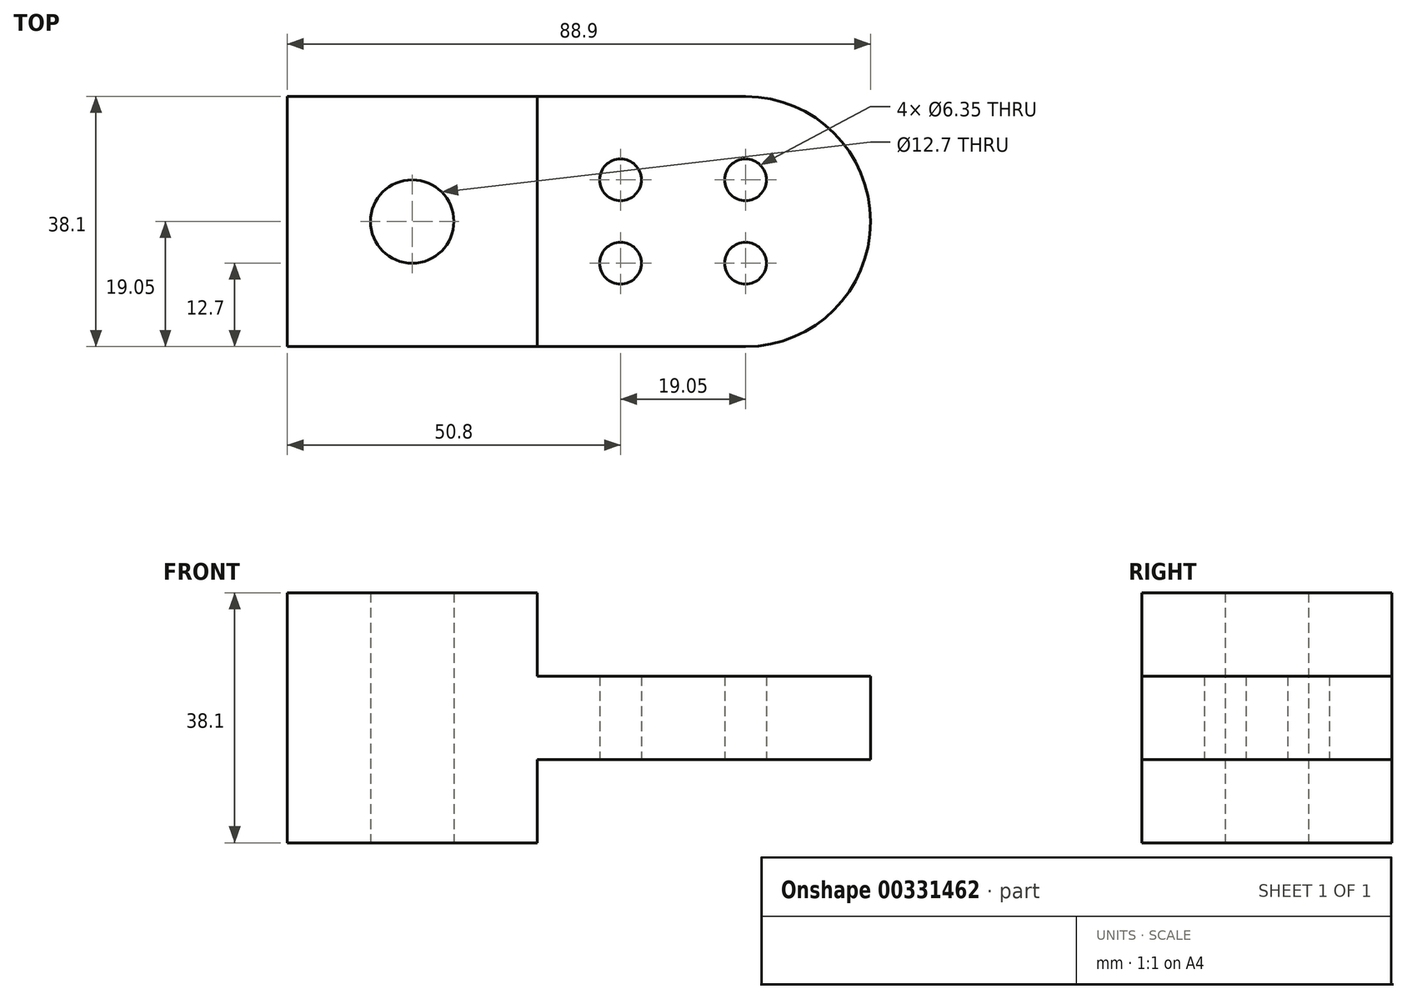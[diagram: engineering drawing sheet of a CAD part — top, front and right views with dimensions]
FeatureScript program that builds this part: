
annotation { "Feature Type Name" : "Feature", "Feature Type Description" : "" }
export const myFeature = defineFeature(function(context is Context, id is Id, definition is map)
    precondition{}
    {
        {
            var Q0;
            Q0=qCreatedBy(makeId("Top.planeOp"),FACE);
            var sketch = newSketch(context, id + "F0", { "sketchPlane" : qUnion([Q0])});
            skLineSegment(sketch, "E0", {"start": v(0, 0) * mm, "end": v(0, 38.1) * mm});
            skLineSegment(sketch, "E1", {"start": v(0, 38.1) * mm, "end": v(38.1, 38.1) * mm});
            skLineSegment(sketch, "E2", {"start": v(38.1, 38.1) * mm, "end": v(38.1, 0) * mm});
            skLineSegment(sketch, "E3", {"start": v(38.1, 0) * mm, "end": v(0, 0) * mm});
            skLineSegment(sketch, "E4", {"start": v(38.1, 38.1) * mm, "end": v(69.85, 38.1) * mm});
            skLineSegment(sketch, "E5", {"start": v(38.1, 0) * mm, "end": v(69.85, 0) * mm});
            skLineSegment(sketch, "E6", {"start": v(69.85, 9.53) * mm, "end": v(69.85, 15.88) * mm, "construction": true});
            skArc(sketch, "E7", {"start": v(69.85, 0) * mm, "mid": v(88.9, 19.05) * mm, "end": v(69.85, 38.1) * mm});
            skLineSegment(sketch, "E8", {"start": v(19.05, 0) * mm, "end": v(19.05, 38.1) * mm, "construction": true});
            skCircle(sketch, "E9", {"center": v(19.05, 19.05) * mm, "radius": 6.35 * mm});
            skLineSegment(sketch, "E10", {"start": v(50.8, 38.1) * mm, "end": v(50.8, 9.53) * mm, "construction": true});
            skCircle(sketch, "E11", {"center": v(50.8, 25.4) * mm, "radius": 3.18 * mm});
            skCircle(sketch, "E12", {"center": v(69.85, 25.4) * mm, "radius": 3.18 * mm});
            skCircle(sketch, "E13", {"center": v(69.85, 12.7) * mm, "radius": 3.18 * mm});
            skCircle(sketch, "E14", {"center": v(50.8, 12.7) * mm, "radius": 3.18 * mm});
            skPoint(sketch, "E15.orphan", {"position": v(50.8, 0) * mm});
            skLineSegment(sketch, "E16.trimOffspring", {"start": v(69.85, 22.23) * mm, "end": v(69.85, 28.58) * mm, "construction": true});
            skSolve(sketch);
        }
        {
            var Q0;
            Q0 = qSketchRegion(id + "F0", true);
            extrude(context, id + "F1", {"entities" : qUnion([Q0]), "depth" : 12.7 * mm});
        }
        {
            var Q0;
            Q0=makeQuery(id+"F1.opExtrude","CAP_FACE",FACE,{"disambiguationData":[OSD([sQuery(id+"F0.wireOp",EDGE,"E0"),sQuery(id+"F0.wireOp",EDGE,"E1"),sQuery(id+"F0.wireOp",EDGE,"E3"),sQuery(id+"F0.wireOp",EDGE,"E4"),sQuery(id+"F0.wireOp",EDGE,"E5"),sQuery(id+"F0.wireOp",EDGE,"E7"),sQuery(id+"F0.wireOp",EDGE,"E9"),sQuery(id+"F0.wireOp",EDGE,"E11"),sQuery(id+"F0.wireOp",EDGE,"E12"),sQuery(id+"F0.wireOp",EDGE,"E13"),sQuery(id+"F0.wireOp",EDGE,"E14")])],"isStart":false});
            var sketch = newSketch(context, id + "F2", { "sketchPlane" : qUnion([Q0])});
            skLineSegment(sketch, "E17", {"start": v(38.1, 38.1) * mm, "end": v(38.1, 0) * mm});
            skSolve(sketch);
        }
        {
            var Q0;
            Q0 = qSketchRegion(id + "F2", true);
            var Q1;
            {var subQ2=sQuery(id+"F2.wireOp",EDGE,"E17");Q1=makeQuery(id+"F2.imprint","IMPRINT",FACE,{"disambiguationData":[TD([[makeQuery(id+"F2.imprint","IMPRINT",EDGE,{"derivedFrom":subQ2}),-1.0]])]});}
            extrude(context, id + "F3", {"entities" : qUnion([Q0, Q1]), "operationType" : NewBodyOperationType.ADD, "depth" : 12.7 * mm});
        }
        {
            var Q0;
            Q0=makeQuery(id+"F1.opExtrude","CAP_FACE",FACE,{"disambiguationData":[OSD([sQuery(id+"F0.wireOp",EDGE,"E0"),sQuery(id+"F0.wireOp",EDGE,"E1"),sQuery(id+"F0.wireOp",EDGE,"E3"),sQuery(id+"F0.wireOp",EDGE,"E4"),sQuery(id+"F0.wireOp",EDGE,"E5"),sQuery(id+"F0.wireOp",EDGE,"E7"),sQuery(id+"F0.wireOp",EDGE,"E9"),sQuery(id+"F0.wireOp",EDGE,"E11"),sQuery(id+"F0.wireOp",EDGE,"E12"),sQuery(id+"F0.wireOp",EDGE,"E13"),sQuery(id+"F0.wireOp",EDGE,"E14")])],"isStart":true});
            var sketch = newSketch(context, id + "F4", { "sketchPlane" : qUnion([Q0])});
            skLineSegment(sketch, "E18", {"start": v(38.1, 0) * mm, "end": v(38.1, -38.1) * mm});
            skSolve(sketch);
        }
        {
            var Q0;
            Q0 = qSketchRegion(id + "F4", true);
            var Q1;
            {var subQ2=sQuery(id+"F4.wireOp",EDGE,"E18");Q1=makeQuery(id+"F4.imprint","IMPRINT",FACE,{"disambiguationData":[TD([[makeQuery(id+"F4.imprint","IMPRINT",EDGE,{"derivedFrom":subQ2}),-1.0]])]});}
            extrude(context, id + "F5", {"entities" : qUnion([Q0, Q1]), "operationType" : NewBodyOperationType.ADD, "depth" : 12.7 * mm});
        }
    });
